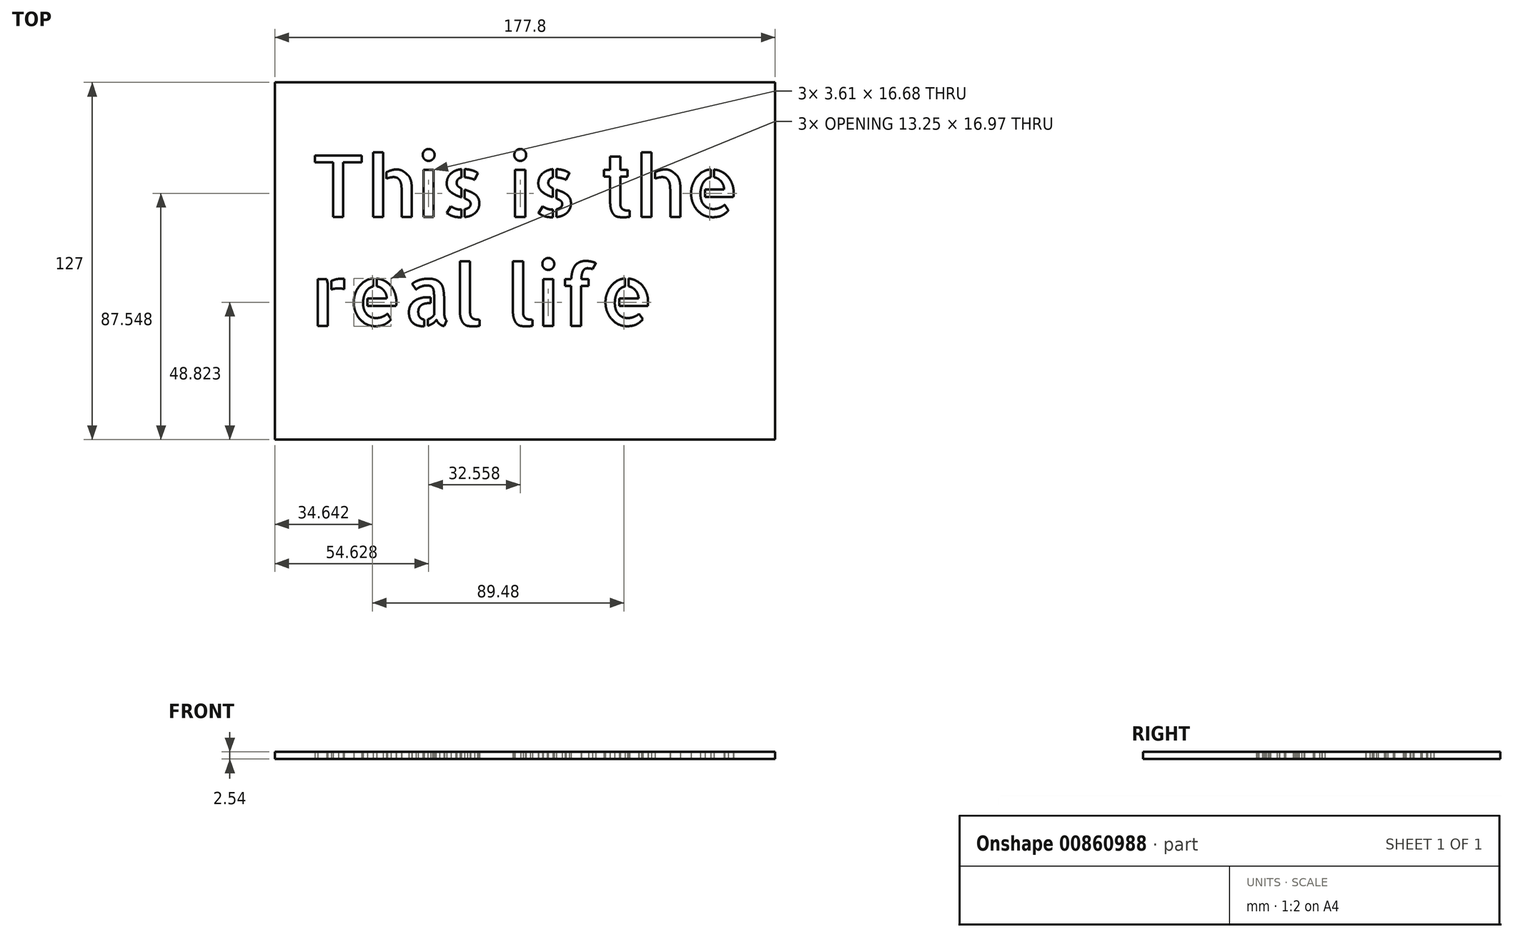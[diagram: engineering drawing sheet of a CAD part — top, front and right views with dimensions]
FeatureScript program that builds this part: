
annotation { "Feature Type Name" : "Feature", "Feature Type Description" : "" }
export const myFeature = defineFeature(function(context is Context, id is Id, definition is map)
    precondition{}
    {
        {
            var Q0;
            Q0=qCreatedBy(makeId("Top.planeOp"),FACE);
            var sketch = newSketch(context, id + "F0", { "sketchPlane" : qUnion([Q0])});
            skLineSegment(sketch, "E0.bottom", {"start": v(-86.25, 68.32) * mm, "end": v(91.55, 68.32) * mm});
            skLineSegment(sketch, "E0.top", {"start": v(-86.25, -58.68) * mm, "end": v(91.55, -58.68) * mm});
            skLineSegment(sketch, "E0.left", {"start": v(-86.25, 68.32) * mm, "end": v(-86.25, -58.68) * mm});
            skLineSegment(sketch, "E0.right", {"start": v(91.55, 68.32) * mm, "end": v(91.55, -58.68) * mm});
            skSolve(sketch);
        }
        {
            var Q0;
            Q0=makeQuery(id+"F0.imprint","IMPRINT",FACE,{"disambiguationData":[TD([[makeQuery(id+"F0.imprint","IMPRINT",EDGE,{"derivedFrom":sQuery(id+"F0.wireOp",EDGE,"E0.bottom")}),-1.0]])]});
            extrude(context, id + "F1", {"entities" : qUnion([Q0]), "depth" : 2.54 * mm, "offsetDistance" : 25.4 * mm});
        }
        {
            var Q0;
            Q0=qCreatedBy(makeId("Top.planeOp"),FACE);
            var sketch = newSketch(context, id + "F2", { "sketchPlane" : qUnion([Q0])});
            skText(sketch, "E1", { "text": "This is the\nreal life", "fontName": "AllertaStencil-Regular.ttf"});
            skLineSegment(sketch, "E2.0", {"start": v(-86.25, 68.32) * mm, "end": v(-86.25, -58.68) * mm});
            skLineSegment(sketch, "E3.0", {"start": v(91.55, 68.32) * mm, "end": v(91.55, -58.68) * mm});
            const initialGuessF2  = {"E1": [-0.07355, 0.02053, 1, 0, 0.0218]};
            skSetInitialGuess(sketch, initialGuessF2);
            skSolve(sketch);
        }
        {
            var Q0;
            Q0 = qSketchRegion(id + "F2", true);
            extrude(context, id + "F3", {"entities" : qUnion([Q0]), "operationType" : NewBodyOperationType.REMOVE, "endBound" : BoundingType.THROUGH_ALL, "depth" : 25.4 * mm, "offsetDistance" : 25.4 * mm});
        }
    });
